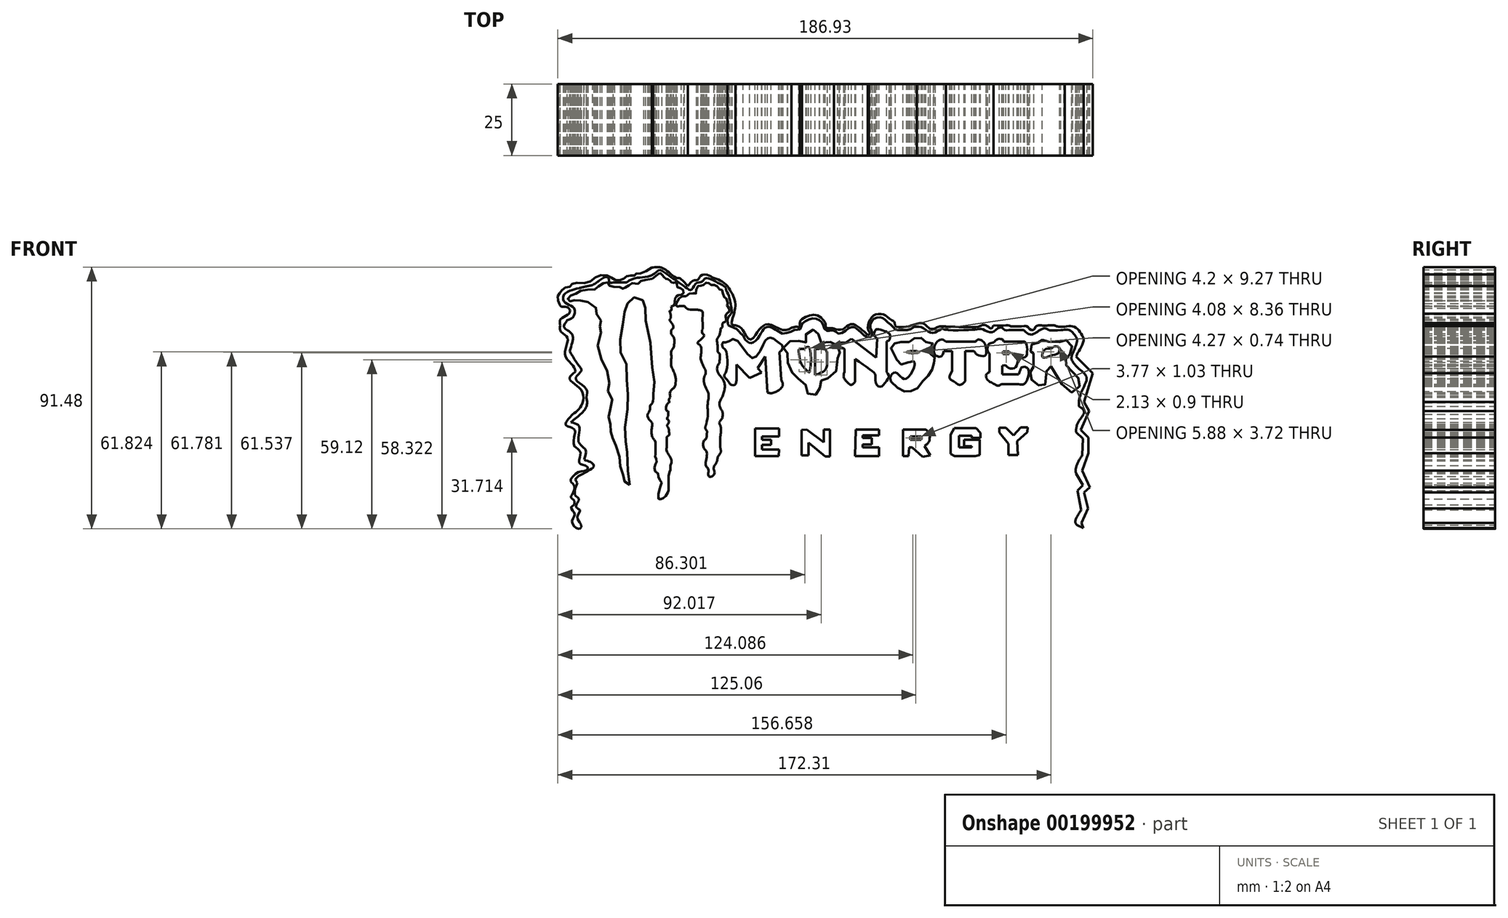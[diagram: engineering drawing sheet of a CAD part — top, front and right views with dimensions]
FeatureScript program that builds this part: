
annotation { "Feature Type Name" : "Feature", "Feature Type Description" : "" }
export const myFeature = defineFeature(function(context is Context, id is Id, definition is map)
    precondition{}
    {
        {
            var Q0;
            Q0=qCreatedBy(makeId("Front.planeOp"),FACE);
            var sketch = newSketch(context, id + "F0", { "sketchPlane" : qUnion([Q0])});
            skLineSegment(sketch, "E0.bottom", {"start": v(-137.52, -64.74) * mm, "end": v(-131.73, -64.74) * mm});
            skLineSegment(sketch, "E0.top", {"start": v(-137.52, -68.4) * mm, "end": v(-131.73, -68.4) * mm});
            skLineSegment(sketch, "E0.left", {"start": v(-137.52, -64.74) * mm, "end": v(-137.52, -68.4) * mm});
            skLineSegment(sketch, "E0.right", {"start": v(-131.73, -64.74) * mm, "end": v(-131.73, -68.4) * mm});
            skSolve(sketch);
        }
        {
            var Q0;
            Q0 = qConstructionFilter(qBodyType(qCreatedBy(id + "F0" ,EDGE), BodyType.WIRE), ConstructionObject.NO);
            extrude(context, id + "F1", {"bodyType" : ToolBodyType.SURFACE, "surfaceEntities" : qUnion([Q0]), "depth" : 25 * mm});
        }
        {
            var Q0;
            Q0=qCreatedBy(makeId("Front.planeOp"),FACE);
            var sketch = newSketch(context, id + "F2", { "sketchPlane" : qUnion([Q0])});
            skPoint(sketch, "E1.start.orphan", {"position": v(0, -27.28) * mm});
            skLineSegment(sketch, "E2", {"start": v(-13.64, -32.05) * mm, "end": v(-21.83, -32.05) * mm});
            skLineSegment(sketch, "E3", {"start": v(-21.83, -32.05) * mm, "end": v(-21.83, -22.36) * mm});
            skLineSegment(sketch, "E4", {"start": v(-21.83, -22.36) * mm, "end": v(-13.54, -22.36) * mm});
            skLineSegment(sketch, "E5", {"start": v(-13.54, -22.36) * mm, "end": v(-13.54, -25.1) * mm});
            skLineSegment(sketch, "E6", {"start": v(-13.54, -25.1) * mm, "end": v(-19.44, -25.1) * mm});
            skLineSegment(sketch, "E7", {"start": v(-19.44, -25.1) * mm, "end": v(-19.44, -26.35) * mm});
            skLineSegment(sketch, "E8", {"start": v(-19.44, -26.35) * mm, "end": v(-16.23, -26.35) * mm});
            skLineSegment(sketch, "E9", {"start": v(-16.23, -26.35) * mm, "end": v(-16.23, -28.11) * mm});
            skLineSegment(sketch, "E10", {"start": v(-16.23, -28.11) * mm, "end": v(-19.44, -28.11) * mm});
            skLineSegment(sketch, "E11", {"start": v(-19.44, -28.11) * mm, "end": v(-19.44, -29.77) * mm});
            skLineSegment(sketch, "E12", {"start": v(-19.44, -29.77) * mm, "end": v(-13.54, -29.77) * mm});
            skLineSegment(sketch, "E13", {"start": v(-13.54, -29.77) * mm, "end": v(-13.64, -32.05) * mm});
            skLineSegment(sketch, "E14", {"start": v(-5.6, -22.83) * mm, "end": v(-5.6, -31.7) * mm});
            skLineSegment(sketch, "E15", {"start": v(-5.6, -31.7) * mm, "end": v(-3.2, -31.7) * mm});
            skLineSegment(sketch, "E16", {"start": v(-3.2, -31.7) * mm, "end": v(-3.2, -27.34) * mm});
            skLineSegment(sketch, "E17", {"start": v(-3.2, -27.34) * mm, "end": v(2.65, -32.16) * mm});
            skLineSegment(sketch, "E18", {"start": v(2.65, -32.16) * mm, "end": v(4.3, -32.16) * mm});
            skLineSegment(sketch, "E19", {"start": v(4.3, -32.16) * mm, "end": v(4.3, -22.78) * mm});
            skLineSegment(sketch, "E20", {"start": v(4.3, -22.78) * mm, "end": v(2.08, -22.78) * mm});
            skLineSegment(sketch, "E21", {"start": v(2.08, -22.78) * mm, "end": v(2.08, -27.18) * mm});
            skLineSegment(sketch, "E22", {"start": v(2.08, -27.18) * mm, "end": v(-3.83, -22.78) * mm});
            skLineSegment(sketch, "E23", {"start": v(-3.83, -22.78) * mm, "end": v(-5.6, -22.83) * mm});
            skLineSegment(sketch, "E24", {"start": v(13.32, -22.72) * mm, "end": v(21.38, -22.72) * mm});
            skLineSegment(sketch, "E25", {"start": v(21.38, -22.72) * mm, "end": v(21.38, -24.8) * mm});
            skLineSegment(sketch, "E26", {"start": v(21.38, -24.8) * mm, "end": v(15.7, -24.8) * mm});
            skLineSegment(sketch, "E27", {"start": v(15.7, -24.8) * mm, "end": v(15.7, -25.63) * mm});
            skLineSegment(sketch, "E28", {"start": v(15.7, -25.63) * mm, "end": v(18.9, -25.63) * mm});
            skLineSegment(sketch, "E29", {"start": v(18.9, -25.63) * mm, "end": v(18.9, -27.9) * mm});
            skLineSegment(sketch, "E30", {"start": v(18.9, -27.9) * mm, "end": v(15.78, -27.9) * mm});
            skLineSegment(sketch, "E31", {"start": v(15.78, -27.9) * mm, "end": v(15.78, -28.91) * mm});
            skLineSegment(sketch, "E32", {"start": v(15.78, -28.91) * mm, "end": v(21.38, -28.91) * mm});
            skLineSegment(sketch, "E33", {"start": v(21.38, -28.91) * mm, "end": v(21.38, -32.03) * mm});
            skLineSegment(sketch, "E34", {"start": v(21.38, -32.03) * mm, "end": v(13.11, -32.03) * mm});
            skLineSegment(sketch, "E35", {"start": v(13.11, -32.03) * mm, "end": v(13.32, -22.72) * mm});
            skLineSegment(sketch, "E36", {"start": v(31.73, -32.05) * mm, "end": v(29.87, -32.05) * mm});
            skLineSegment(sketch, "E37", {"start": v(29.87, -32.05) * mm, "end": v(29.87, -22.72) * mm});
            skLineSegment(sketch, "E38", {"start": v(29.87, -22.72) * mm, "end": v(37.84, -22.72) * mm});
            skFitSpline(sketch, "E39", {"points": [v(37.84, -22.72) * mm, v(39.06, -24.2) * mm, v(39.12, -25.83) * mm, v(38.77, -27.23) * mm, v(37.31, -28.45) * mm], "startDerivative": vector(5.78, -5.29) * mm, "endDerivative": vector(-6.62, -4.3) * mm});
            skLineSegment(sketch, "E40", {"start": v(37.31, -28.45) * mm, "end": v(39.3, -31.77) * mm});
            skLineSegment(sketch, "E41", {"start": v(39.3, -31.77) * mm, "end": v(36.67, -32.23) * mm});
            skLineSegment(sketch, "E42", {"start": v(36.67, -32.23) * mm, "end": v(32.95, -28.92) * mm});
            skLineSegment(sketch, "E43", {"start": v(32.95, -28.92) * mm, "end": v(32.02, -28.92) * mm});
            skLineSegment(sketch, "E44", {"start": v(32.02, -28.92) * mm, "end": v(31.73, -32.05) * mm});
            skLineSegment(sketch, "E45", {"start": v(55.12, -32.05) * mm, "end": v(47.86, -32.05) * mm});
            skLineSegment(sketch, "E46", {"start": v(47.86, -32.05) * mm, "end": v(46.4, -31.25) * mm});
            skLineSegment(sketch, "E47", {"start": v(46.4, -31.25) * mm, "end": v(46.4, -24.47) * mm});
            skLineSegment(sketch, "E48", {"start": v(46.4, -24.47) * mm, "end": v(47.68, -22.16) * mm});
            skLineSegment(sketch, "E49", {"start": v(47.68, -22.16) * mm, "end": v(55.4, -22.16) * mm});
            skLineSegment(sketch, "E50", {"start": v(55.4, -22.16) * mm, "end": v(56.85, -23.85) * mm});
            skLineSegment(sketch, "E51", {"start": v(56.85, -23.85) * mm, "end": v(56.85, -25.72) * mm});
            skLineSegment(sketch, "E52", {"start": v(56.85, -25.72) * mm, "end": v(53.88, -25.72) * mm});
            skLineSegment(sketch, "E53", {"start": v(53.88, -25.72) * mm, "end": v(53.88, -24.92) * mm});
            skLineSegment(sketch, "E54", {"start": v(53.88, -24.92) * mm, "end": v(49.44, -24.92) * mm});
            skLineSegment(sketch, "E55", {"start": v(49.44, -24.92) * mm, "end": v(49.44, -29) * mm});
            skLineSegment(sketch, "E56", {"start": v(49.44, -29) * mm, "end": v(53.88, -29) * mm});
            skLineSegment(sketch, "E57", {"start": v(53.88, -29) * mm, "end": v(53.88, -28.55) * mm});
            skLineSegment(sketch, "E58", {"start": v(53.88, -28.55) * mm, "end": v(51.18, -28.55) * mm});
            skLineSegment(sketch, "E59", {"start": v(51.18, -28.55) * mm, "end": v(51.18, -26.3) * mm});
            skLineSegment(sketch, "E60", {"start": v(51.18, -26.3) * mm, "end": v(56.62, -26.3) * mm});
            skLineSegment(sketch, "E61", {"start": v(56.62, -26.3) * mm, "end": v(56.62, -31.63) * mm});
            skLineSegment(sketch, "E62", {"start": v(56.62, -31.63) * mm, "end": v(55.12, -32.05) * mm});
            skLineSegment(sketch, "E63", {"start": v(69.9, -31.63) * mm, "end": v(66.64, -31.63) * mm});
            skLineSegment(sketch, "E64", {"start": v(66.64, -31.63) * mm, "end": v(66.64, -27.74) * mm});
            skLineSegment(sketch, "E65", {"start": v(66.64, -27.74) * mm, "end": v(63.46, -23.72) * mm});
            skLineSegment(sketch, "E66", {"start": v(63.46, -23.72) * mm, "end": v(63.46, -22.15) * mm});
            skLineSegment(sketch, "E67", {"start": v(63.46, -22.15) * mm, "end": v(65.72, -22.15) * mm});
            skLineSegment(sketch, "E68", {"start": v(65.72, -22.15) * mm, "end": v(68.42, -24.71) * mm});
            skLineSegment(sketch, "E69", {"start": v(68.42, -24.71) * mm, "end": v(70.99, -22) * mm});
            skLineSegment(sketch, "E70", {"start": v(70.99, -22) * mm, "end": v(73.33, -22) * mm});
            skLineSegment(sketch, "E71", {"start": v(73.33, -22) * mm, "end": v(73.2, -23.63) * mm});
            skLineSegment(sketch, "E72", {"start": v(73.2, -23.63) * mm, "end": v(69.74, -26.81) * mm});
            skLineSegment(sketch, "E73", {"start": v(69.74, -26.81) * mm, "end": v(69.9, -31.63) * mm});
            skLineSegment(sketch, "E74.bottom", {"start": v(32.38, -25.2) * mm, "end": v(36.14, -25.2) * mm});
            skLineSegment(sketch, "E74.top", {"start": v(32.38, -26.23) * mm, "end": v(36.14, -26.23) * mm});
            skLineSegment(sketch, "E74.left", {"start": v(32.38, -25.2) * mm, "end": v(32.38, -26.23) * mm});
            skLineSegment(sketch, "E74.right", {"start": v(36.14, -25.2) * mm, "end": v(36.14, -26.23) * mm});
            skFitSpline(sketch, "E75", {"points": [v(3.5, -4.78) * mm, v(1.8, -5.19) * mm, v(0.6, -6.8) * mm, v(0.68, -9.22) * mm, v(-1.5, -10.84) * mm, v(-3.52, -10.03) * mm, v(-4.24, -6.96) * mm, v(-6.9, -4.86) * mm, v(-9, -2.69) * mm, v(-10.54, 1.1) * mm, v(-10.62, 4.25) * mm, v(-11.83, 5.63) * mm, v(-11.9, 6.51) * mm, v(-7.3, 8.77) * mm, v(-6.02, 7.64) * mm, v(-3.92, 7.97) * mm, v(-4.08, 10.7) * mm, v(-1.81, 12.14) * mm, v(0, 11.62) * mm, v(0.62, 8.04) * mm, v(3.37, 7.78) * mm, v(5.87, 7.52) * mm, v(7.54, 5.47) * mm, v(7.73, 4.13) * mm, v(7.09, 3.43) * mm, v(6.83, -1.5) * mm, v(3.5, -4.78) * mm]});
            skFitSpline(sketch, "E76", {"points": [v(-3.3, -2.5) * mm, v(-5.32, -0.43) * mm, v(-6.25, 1.83) * mm, v(-6.53, 4.09) * mm, v(-6.49, 5.34) * mm, v(-4.71, 5.46) * mm, v(-4.1, 5.94) * mm, v(-2.94, 5.94) * mm, v(-2.86, -2.65) * mm, v(-3.3, -2.5) * mm]});
            skLineSegment(sketch, "E77", {"start": v(-0.88, 5.34) * mm, "end": v(-0.88, -3.74) * mm});
            skFitSpline(sketch, "E78", {"points": [v(-0.88, -3.74) * mm, v(1.82, -2.53) * mm, v(3.07, -1.04) * mm, v(3.32, 2.51) * mm, v(3.2, 4.4) * mm, v(2.59, 5.38) * mm, v(0.98, 5.54) * mm, v(-0.88, 5.34) * mm], "startDerivative": vector(17.33, 6.66) * mm, "endDerivative": vector(-13.48, -1.69) * mm});
            skLineSegment(sketch, "E79", {"start": v(13, 1.9) * mm, "end": v(13, -6.13) * mm});
            skFitSpline(sketch, "E80", {"points": [v(13, -6.13) * mm, v(11.7, -7.08) * mm, v(9.88, -5.7) * mm, v(9.07, -4.24) * mm, v(9.32, -2.56) * mm], "startDerivative": vector(-5.12, -6.15) * mm, "endDerivative": vector(2, 7.23) * mm});
            skLineSegment(sketch, "E81", {"start": v(9.32, -2.56) * mm, "end": v(9.32, 4.81) * mm});
            skFitSpline(sketch, "E82", {"points": [v(9.32, 4.81) * mm, v(9.32, 5.45) * mm, v(8.29, 5.83) * mm, v(7.55, 6.15) * mm, v(7.84, 7.43) * mm, v(9.8, 7.56) * mm], "startDerivative": vector(1.21, 4.66) * mm, "endDerivative": vector(8.72, -1.45) * mm});
            skLineSegment(sketch, "E83", {"start": v(9.8, 7.56) * mm, "end": v(11.78, 9.02) * mm});
            skLineSegment(sketch, "E84", {"start": v(11.78, 9.02) * mm, "end": v(20.42, 2.42) * mm});
            skLineSegment(sketch, "E85", {"start": v(20.42, 2.42) * mm, "end": v(20.78, 9.02) * mm});
            skFitSpline(sketch, "E86", {"points": [v(20.78, 9.02) * mm, v(19.76, 10.24) * mm, v(19.97, 11.77) * mm, v(20.78, 12.38) * mm, v(23.58, 11.67) * mm, v(25.2, 10.5) * mm, v(25, 8.52) * mm, v(24.14, 8.16) * mm], "startDerivative": vector(-9.3, 7.78) * mm, "endDerivative": vector(-8.95, -0.97) * mm});
            skLineSegment(sketch, "E87", {"start": v(24.14, 8.16) * mm, "end": v(24.14, -2.67) * mm});
            skFitSpline(sketch, "E88", {"points": [v(24.14, -2.67) * mm, v(24.85, -4.1) * mm, v(23.68, -6.23) * mm, v(22.05, -7.75) * mm, v(20.48, -6.84) * mm, v(20.17, -3.84) * mm, v(19.5, -2.67) * mm, v(13, 1.9) * mm], "startDerivative": vector(9.85, -12.2) * mm, "endDerivative": vector(-32.83, 21.87) * mm});
            skFitSpline(sketch, "E89", {"points": [v(25.58, -6) * mm, v(25.5, -4.1) * mm, v(27.4, -2.82) * mm, v(30.6, -5.05) * mm, v(33.92, 0.65) * mm, v(31.55, 0.71) * mm], "startDerivative": vector(-3.3, 12.09) * mm, "endDerivative": vector(-18.92, -5.85) * mm});
            skFitSpline(sketch, "E90", {"points": [v(31.55, 0.71) * mm, v(29.32, 0) * mm, v(27.8, 1.3) * mm, v(26.98, 3.23) * mm, v(25.76, 4.9) * mm, v(25.92, 6.69) * mm, v(27.5, 7.6) * mm, v(29.52, 7.86) * mm, v(32.52, 8.11) * mm, v(33.92, 9.28) * mm, v(36.28, 9.28) * mm, v(37.6, 7.9) * mm, v(39.84, 7.65) * mm, v(40.15, 5.98) * mm, v(38.57, 4.66) * mm, v(39.7, 3.64) * mm, v(40.96, 2.11) * mm, v(40.7, 0.71) * mm, v(40.1, -1.24) * mm, v(38.98, -3.43) * mm, v(37, -5.46) * mm, v(34.96, -8.1) * mm, v(32.83, -9.17) * mm, v(30.8, -9.48) * mm, v(28.36, -8.5) * mm, v(25.58, -6) * mm], "startDerivative": vector(-56.1, -30.21) * mm, "endDerivative": vector(-52.2, 53.3) * mm});
            skLineSegment(sketch, "E91", {"start": v(51.53, -5.87) * mm, "end": v(51.53, 4.76) * mm});
            skLineSegment(sketch, "E92", {"start": v(51.53, 4.76) * mm, "end": v(54.58, 4.76) * mm});
            skFitSpline(sketch, "E93", {"points": [v(54.58, 4.76) * mm, v(56, 3.33) * mm, v(58.55, 3.23) * mm, v(58.85, 5.27) * mm, v(58.4, 7.3) * mm, v(57.53, 8.26) * mm, v(56.1, 8.77) * mm, v(55.24, 8.01) * mm], "startDerivative": vector(7.12, -10.63) * mm, "endDerivative": vector(-6.49, -9.06) * mm});
            skLineSegment(sketch, "E94", {"start": v(55.24, 8.01) * mm, "end": v(44.82, 8.01) * mm});
            skFitSpline(sketch, "E95", {"points": [v(44.82, 8.01) * mm, v(43.4, 8.77) * mm, v(41.83, 8.01) * mm, v(40.91, 6.69) * mm, v(40.7, 5.47) * mm, v(40.8, 3.69) * mm, v(41.98, 2.83) * mm, v(43.25, 2.88) * mm, v(44.06, 4.7) * mm], "startDerivative": vector(-10.85, 8.8) * mm, "endDerivative": vector(4.19, 16.26) * mm});
            skLineSegment(sketch, "E96", {"start": v(44.06, 4.7) * mm, "end": v(46.9, 4.7) * mm});
            skLineSegment(sketch, "E97", {"start": v(46.9, 4.7) * mm, "end": v(46.9, -2.1) * mm});
            skLineSegment(sketch, "E98", {"start": v(46.9, -2.1) * mm, "end": v(46.15, -3.78) * mm});
            skFitSpline(sketch, "E99", {"points": [v(46.15, -3.78) * mm, v(46.15, -4.9) * mm, v(47.57, -5.92) * mm, v(49.7, -7.09) * mm, v(51.53, -5.87) * mm], "startDerivative": vector(-1.29, -6.23) * mm, "endDerivative": vector(6.5, 6.73) * mm});
            skEllipse(sketch, "E100", {"center": v(33.29, 4.35) * mm, "majorRadius": 2.13 * mm, "minorRadius": 0.37 * mm, "majorAxis": v(-1, 0)});
            skLineSegment(sketch, "E101", {"start": v(60.02, -2.61) * mm, "end": v(60.02, 3.8) * mm});
            skFitSpline(sketch, "E102", {"points": [v(60.02, 3.8) * mm, v(59.46, 4.6) * mm, v(59.41, 6.33) * mm, v(60.02, 7.35) * mm, v(61.34, 7.7) * mm, v(62.77, 8.77) * mm, v(64.55, 8.77) * mm, v(65, 7.96) * mm], "startDerivative": vector(-5.38, 5.66) * mm, "endDerivative": vector(2.12, -7.98) * mm});
            skLineSegment(sketch, "E103", {"start": v(65, 7.96) * mm, "end": v(72.32, 7.96) * mm});
            skFitSpline(sketch, "E104", {"points": [v(72.32, 7.96) * mm, v(73.09, 6.69) * mm, v(73.19, 4.4) * mm, v(72.68, 2.67) * mm, v(70.65, 2.27) * mm, v(70.24, 2.01) * mm, v(69.32, -0.68) * mm, v(68.46, -1.34) * mm, v(66.68, -1.19) * mm, v(65.82, -0.38) * mm, v(64.55, -0.43) * mm], "startDerivative": vector(9.43, -11.65) * mm, "endDerivative": vector(-15.75, -3.65) * mm});
            skLineSegment(sketch, "E105", {"start": v(64.55, -0.43) * mm, "end": v(64.55, -3.38) * mm});
            skLineSegment(sketch, "E106", {"start": v(64.55, -3.38) * mm, "end": v(70.19, -3.38) * mm});
            skFitSpline(sketch, "E107", {"points": [v(70.19, -3.38) * mm, v(70.8, -1.95) * mm, v(71.36, -0.99) * mm, v(73.09, -1.04) * mm, v(73.75, -2.61) * mm, v(73.29, -5.05) * mm, v(72.73, -6.22) * mm, v(71.71, -6.98) * mm, v(70.19, -6.83) * mm], "startDerivative": vector(5.45, 11.63) * mm, "endDerivative": vector(-12.95, 3.3) * mm});
            skLineSegment(sketch, "E108", {"start": v(70.19, -6.83) * mm, "end": v(64.34, -6.83) * mm});
            skFitSpline(sketch, "E109", {"points": [v(64.34, -6.83) * mm, v(62.97, -7.4) * mm, v(61.75, -6.83) * mm, v(59.51, -5.51) * mm, v(58.85, -3.73) * mm, v(60.02, -2.61) * mm], "startDerivative": vector(-7.82, -4.67) * mm, "endDerivative": vector(8.05, 4.95) * mm});
            skLineSegment(sketch, "E110.bottom", {"start": v(64.8, 4.56) * mm, "end": v(66.92, 4.56) * mm});
            skLineSegment(sketch, "E110.top", {"start": v(64.8, 3.66) * mm, "end": v(66.92, 3.66) * mm});
            skLineSegment(sketch, "E110.left", {"start": v(64.8, 4.56) * mm, "end": v(64.8, 3.66) * mm});
            skLineSegment(sketch, "E110.right", {"start": v(66.92, 4.56) * mm, "end": v(66.92, 3.66) * mm});
            skFitSpline(sketch, "E111", {"points": [v(75.4, 3.92) * mm, v(75.17, 4.58) * mm, v(74.49, 4.56) * mm, v(74.3, 6.2) * mm, v(75.86, 7.6) * mm, v(77.08, 7.64) * mm, v(77.48, 8.3) * mm, v(79.77, 8.47) * mm, v(80.47, 8) * mm, v(84.73, 7.96) * mm, v(86.3, 8.64) * mm, v(88.87, 6.8) * mm, v(88.27, 4.41) * mm, v(87.85, 2.62) * mm, v(86.44, 1.76) * mm, v(86.4, 0.4) * mm, v(92.16, -6.53) * mm, v(90.32, -8.41) * mm, v(87.72, -9.74) * mm, v(80.66, 0) * mm, v(79.72, -6.02) * mm, v(78.66, -7.6) * mm, v(76.05, -6.61) * mm, v(74.34, -4.48) * mm, v(74.38, -2.51) * mm, v(75.1, -1.91) * mm, v(75.4, 3.92) * mm]});
            skFitSpline(sketch, "E112", {"points": [v(78.57, 2.53) * mm, v(79.51, 5.35) * mm, v(81.65, 5.7) * mm, v(82.67, 6.34) * mm, v(84.17, 6) * mm, v(84.51, 5.05) * mm, v(84, 3.92) * mm, v(81.86, 3.22) * mm, v(78.57, 2.53) * mm]});
            skLineSegment(sketch, "E113", {"start": v(-28.35, -5.42) * mm, "end": v(-28.35, 0) * mm});
            skLineSegment(sketch, "E114", {"start": v(-28.35, 0) * mm, "end": v(-23.74, -4.68) * mm});
            skLineSegment(sketch, "E115", {"start": v(-23.74, -4.68) * mm, "end": v(-19.53, -2.78) * mm});
            skLineSegment(sketch, "E116", {"start": v(-19.53, -2.78) * mm, "end": v(-20.95, -1.22) * mm});
            skLineSegment(sketch, "E117", {"start": v(-20.95, -1.22) * mm, "end": v(-18.38, 2.79) * mm});
            skLineSegment(sketch, "E118", {"start": v(-18.38, 2.79) * mm, "end": v(-17.56, -9.83) * mm});
            skFitSpline(sketch, "E119", {"points": [v(-17.56, -9.83) * mm, v(-15.26, -9.83) * mm, v(-12.27, -7.46) * mm, v(-12.74, -5.29) * mm], "startDerivative": vector(6.9, -1.35) * mm, "endDerivative": vector(-3.74, 7.1) * mm});
            skLineSegment(sketch, "E120", {"start": v(-12.74, -5.29) * mm, "end": v(-13.36, 4.28) * mm});
            skFitSpline(sketch, "E121", {"points": [v(-13.36, 4.28) * mm, v(-12.31, 5.41) * mm, v(-12.48, 6.8) * mm, v(-13.6, 7.67) * mm, v(-15.8, 9.2) * mm, v(-17.42, 9.14) * mm, v(-18.93, 7.26) * mm, v(-22.71, 2.19) * mm, v(-28.88, 8.87) * mm, v(-31.87, 7.72) * mm, v(-33.08, 7.78) * mm, v(-33.44, 6.51) * mm, v(-32.32, 5.27) * mm], "startDerivative": vector(20.04, 15.2) * mm, "endDerivative": vector(21.72, -15.34) * mm});
            skFitSpline(sketch, "E122", {"points": [v(-32.32, 5.27) * mm, v(-31.8, 4) * mm, v(-31.91, -2.31) * mm, v(-32.7, -4.07) * mm, v(-31.49, -5.46) * mm, v(-30.43, -6.92) * mm, v(-28.94, -7.06) * mm, v(-28.35, -5.42) * mm], "startDerivative": vector(5, -7.8) * mm, "endDerivative": vector(2, 15.9) * mm});
            skFitSpline(sketch, "E123", {"points": [v(86.28, 13.2) * mm, v(89.51, 13.26) * mm, v(91.89, 11.04) * mm, v(92.9, 8.45) * mm, v(91.1, 4.42) * mm, v(90.3, 2.84) * mm], "startDerivative": vector(16.55, 3.2) * mm, "endDerivative": vector(-3.97, -8.8) * mm});
            skLineSegment(sketch, "E124", {"start": v(90.3, 2.84) * mm, "end": v(96.13, -3.05) * mm});
            skLineSegment(sketch, "E125", {"start": v(96.13, -3.05) * mm, "end": v(93.1, -13.12) * mm});
            skLineSegment(sketch, "E126", {"start": v(93.1, -13.12) * mm, "end": v(94.83, -16.28) * mm});
            skLineSegment(sketch, "E127", {"start": v(94.83, -16.28) * mm, "end": v(91.89, -22.9) * mm});
            skLineSegment(sketch, "E128", {"start": v(91.89, -22.9) * mm, "end": v(94.62, -25.48) * mm});
            skLineSegment(sketch, "E129", {"start": v(94.62, -25.48) * mm, "end": v(94.62, -31.02) * mm});
            skLineSegment(sketch, "E130", {"start": v(94.62, -31.02) * mm, "end": v(92.46, -37.13) * mm});
            skLineSegment(sketch, "E131", {"start": v(92.46, -37.13) * mm, "end": v(95.12, -42.88) * mm});
            skLineSegment(sketch, "E132", {"start": v(95.12, -42.88) * mm, "end": v(93.1, -44.75) * mm});
            skLineSegment(sketch, "E133", {"start": v(93.1, -44.75) * mm, "end": v(94.4, -50.36) * mm});
            skLineSegment(sketch, "E134", {"start": v(94.4, -50.36) * mm, "end": v(92.24, -55.39) * mm});
            skLineSegment(sketch, "E135", {"start": v(92.24, -55.39) * mm, "end": v(92.75, -57.18) * mm});
            skLineSegment(sketch, "E136", {"start": v(92.75, -57.18) * mm, "end": v(90.66, -56.18) * mm});
            skPoint(sketch, "E137.2.internal.snap0", {"position": v(91.7, -56.68) * mm});
            skFitSpline(sketch, "E138", {"points": [v(90.66, -56.18) * mm, v(90.02, -55) * mm, v(92.07, -50.8) * mm], "startDerivative": vector(-2.73, 2.84) * mm, "endDerivative": vector(4.79, 7.46) * mm});
            skLineSegment(sketch, "E139", {"start": v(92.07, -50.8) * mm, "end": v(90.77, -44.03) * mm});
            skLineSegment(sketch, "E140", {"start": v(90.77, -44.03) * mm, "end": v(92.68, -42.14) * mm});
            skLineSegment(sketch, "E141", {"start": v(92.68, -42.14) * mm, "end": v(90.23, -38.07) * mm});
            skFitSpline(sketch, "E142", {"points": [v(90.23, -38.07) * mm, v(90.23, -36.29) * mm, v(90.9, -34.27) * mm, v(92.47, -31.65) * mm], "startDerivative": vector(-0.4, 6.03) * mm, "endDerivative": vector(4.52, 6.94) * mm});
            skLineSegment(sketch, "E143", {"start": v(92.47, -31.65) * mm, "end": v(92.65, -25.9) * mm});
            skLineSegment(sketch, "E144", {"start": v(92.65, -25.9) * mm, "end": v(90.31, -23.64) * mm});
            skFitSpline(sketch, "E145", {"points": [v(90.31, -23.64) * mm, v(90.31, -22.52) * mm, v(90.58, -21.24) * mm], "startDerivative": vector(-0.12, 2.3) * mm, "endDerivative": vector(0.65, 2.5) * mm});
            skFitSpline(sketch, "E146", {"points": [v(90.58, -21.24) * mm, v(91.45, -19.47) * mm, v(93.1, -16.52) * mm, v(91.34, -14.62) * mm], "startDerivative": vector(2.12, 5.59) * mm, "endDerivative": vector(-7.8, 5.1) * mm});
            skPoint(sketch, "E147.3.internal.snap0", {"position": v(93.97, -14.7) * mm});
            skFitSpline(sketch, "E147", {"points": [v(91.34, -14.62) * mm, v(91.34, -12.76) * mm, v(92.2, -9.5) * mm, v(93.97, -5.07) * mm, v(93.23, -3.15) * mm, v(91.34, -1.55) * mm], "startDerivative": vector(-0.57, 10.85) * mm, "endDerivative": vector(-11, 8.15) * mm});
            skFitSpline(sketch, "E148", {"points": [v(91.34, -1.55) * mm, v(88.73, 1.8) * mm, v(89.1, 3.93) * mm], "startDerivative": vector(-6.02, 5.91) * mm, "endDerivative": vector(1.96, 5) * mm});
            skFitSpline(sketch, "E149", {"points": [v(89.1, 3.93) * mm, v(90.31, 6.93) * mm, v(90.58, 8.96) * mm, v(89.5, 10.74) * mm, v(87.92, 12) * mm, v(84.92, 12.06) * mm], "startDerivative": vector(5.9, 13.53) * mm, "endDerivative": vector(-14.9, -1.56) * mm});
            skFitSpline(sketch, "E150", {"points": [v(84.92, 12.06) * mm, v(80.75, 12.06) * mm, v(79.77, 12.62) * mm, v(78.62, 12.5) * mm, v(77.15, 11.75) * mm, v(75.93, 10.93) * mm, v(74.42, 10.46) * mm, v(72.95, 11.18) * mm, v(72.05, 12.06) * mm], "startDerivative": vector(-25.23, -2.35) * mm, "endDerivative": vector(-7.45, 8.11) * mm});
            skFitSpline(sketch, "E151", {"points": [v(72.05, 12.06) * mm, v(69.78, 12.06) * mm, v(67.05, 12.06) * mm, v(65.29, 12.06) * mm, v(64.14, 13.01) * mm, v(62.34, 12.18) * mm, v(60.69, 11.25) * mm, v(58.17, 12.06) * mm, v(56.84, 12.5) * mm, v(54.94, 12.18) * mm], "startDerivative": vector(-18.43, -0.3) * mm, "endDerivative": vector(-18.73, -4.91) * mm});
            skFitSpline(sketch, "E152", {"points": [v(54.94, 12.18) * mm, v(54.07, 12.18) * mm, v(44.44, 12.18) * mm, v(43.36, 12.54) * mm, v(41.74, 11.54) * mm, v(39.4, 11.14) * mm, v(36.35, 13.01) * mm, v(33.73, 13.16) * mm], "startDerivative": vector(-6.06, 0.36) * mm, "endDerivative": vector(-18.64, -2.44) * mm});
            skFitSpline(sketch, "E153", {"points": [v(33.73, 13.16) * mm, v(31.82, 12.18) * mm, v(27.11, 12.18) * mm], "startDerivative": vector(-4.1, -2.92) * mm, "endDerivative": vector(-8.83, 0.73) * mm});
            skFitSpline(sketch, "E154", {"points": [v(27.11, 12.18) * mm, v(25.68, 13.77) * mm, v(23.7, 15.42) * mm, v(22.33, 16.4) * mm, v(20.72, 16.43) * mm, v(19.1, 15.42) * mm, v(18.34, 13.16) * mm, v(18.81, 11.77) * mm, v(19.03, 10.78) * mm, v(18.74, 9.78) * mm, v(17.12, 9.63) * mm, v(14.96, 11.47) * mm, v(13.6, 12.58) * mm, v(12.45, 13.16) * mm, v(10.8, 12.76) * mm], "startDerivative": vector(-16.66, 20.22) * mm, "endDerivative": vector(-24.78, -9.61) * mm});
            skFitSpline(sketch, "E155", {"points": [v(10.8, 12.76) * mm, v(8.9, 11.3) * mm, v(6.91, 10.9) * mm, v(6.15, 11.77) * mm, v(4.05, 11.77) * mm, v(3.2, 11.77) * mm, v(2.23, 12.76) * mm, v(1.63, 14.48) * mm, v(0.42, 15.53) * mm, v(-1.44, 16.14) * mm, v(-3.37, 15.65) * mm, v(-5.31, 14.4) * mm, v(-5.84, 13.16) * mm, v(-6.4, 12.18) * mm, v(-7.73, 12.18) * mm, v(-9.7, 11.34) * mm, v(-12.37, 10.85) * mm], "startDerivative": vector(-23.29, -21.5) * mm, "endDerivative": vector(-35.58, -3.08) * mm});
            skFitSpline(sketch, "E156", {"points": [v(-12.37, 10.85) * mm, v(-14.07, 11.78) * mm, v(-15.4, 12.55) * mm, v(-16.9, 13.15) * mm, v(-18.46, 12.75) * mm, v(-19.88, 10.85) * mm, v(-22.42, 7.75) * mm, v(-24.6, 7.99) * mm, v(-26.09, 10.17) * mm], "startDerivative": vector(-14.95, 8.07) * mm, "endDerivative": vector(-9, 18.37) * mm});
            skFitSpline(sketch, "E157", {"points": [v(-26.09, 10.17) * mm, v(-27.34, 11.38) * mm, v(-28.19, 12.3) * mm, v(-29.96, 13.2) * mm, v(-31.3, 13.68) * mm], "startDerivative": vector(-5.24, 4.7) * mm, "endDerivative": vector(-5.26, 1.84) * mm});
            skFitSpline(sketch, "E158", {"points": [v(-31.3, 13.68) * mm, v(-31.3, 16.42) * mm, v(-30.12, 17.95) * mm, v(-30.12, 19.85) * mm, v(-30.57, 22.1) * mm, v(-31.3, 24.65) * mm, v(-31.94, 26.1) * mm, v(-32.14, 26.83) * mm, v(-33.31, 27.76) * mm], "startDerivative": vector(-3.32, 20.04) * mm, "endDerivative": vector(-13.09, 8.19) * mm});
            skFitSpline(sketch, "E159", {"points": [v(-33.31, 27.76) * mm, v(-35.9, 29.13) * mm, v(-38.27, 30.18) * mm, v(-39.77, 29.74) * mm, v(-40.5, 28.85) * mm, v(-42.1, 28.6) * mm, v(-43.4, 27.07) * mm, v(-44.37, 26.02) * mm, v(-45.58, 26.63) * mm, v(-47.68, 28.08) * mm], "startDerivative": vector(-18.59, 9.55) * mm, "endDerivative": vector(-16.96, 11.38) * mm});
            skFitSpline(sketch, "E160", {"points": [v(-47.68, 28.08) * mm, v(-49.2, 29.17) * mm, v(-50.54, 30.06) * mm, v(-52.6, 31.55) * mm, v(-54.33, 32.76) * mm, v(-55.42, 33) * mm, v(-57, 31.75) * mm, v(-60.22, 30.58) * mm, v(-62.16, 30.38) * mm, v(-64.62, 29.94) * mm, v(-66.68, 28.73) * mm], "startDerivative": vector(-16.76, 12.14) * mm, "endDerivative": vector(-18.17, -13.1) * mm});
            skFitSpline(sketch, "E161", {"points": [v(-66.68, 28.73) * mm, v(-69.1, 28.73) * mm, v(-71.44, 28.73) * mm], "startDerivative": vector(-4.82, 0) * mm, "endDerivative": vector(-4.7, 0) * mm});
            skFitSpline(sketch, "E162", {"points": [v(-71.44, 28.73) * mm, v(-72.73, 28.73) * mm, v(-73.1, 30.22) * mm, v(-74.27, 30.58) * mm, v(-76.12, 29.5) * mm, v(-77.17, 28.73) * mm, v(-78.58, 27.76) * mm], "startDerivative": vector(-10.38, -2.63) * mm, "endDerivative": vector(-8.48, -5.77) * mm});
            skFitSpline(sketch, "E163", {"points": [v(-78.58, 27.76) * mm, v(-81.04, 27.27) * mm, v(-83.4, 26.7) * mm], "startDerivative": vector(-4.91, -0.93) * mm, "endDerivative": vector(-4.72, -1.18) * mm});
            skFitSpline(sketch, "E164", {"points": [v(-83.4, 26.7) * mm, v(-86.22, 25.9) * mm, v(-88.71, 24.26) * mm, v(-88.57, 21.91) * mm, v(-86.65, 20.76) * mm, v(-84.97, 19.37) * mm, v(-85.36, 16.68) * mm, v(-87.47, 15.48) * mm], "startDerivative": vector(-17.93, -4.52) * mm, "endDerivative": vector(-17.34, -5.6) * mm});
            skFitSpline(sketch, "E165", {"points": [v(-87.47, 15.48) * mm, v(-88.57, 12.99) * mm, v(-85.93, 10.78) * mm, v(-86.66, 4.73) * mm], "startDerivative": vector(-7.66, -9.9) * mm, "endDerivative": vector(-5.87, -17.07) * mm});
            skFitSpline(sketch, "E166", {"points": [v(-86.66, 4.73) * mm, v(-83.4, -0.5) * mm, v(-82.62, -2.32) * mm, v(-84.59, -4.81) * mm, v(-80.94, -8.41) * mm, v(-80.85, -11.43) * mm], "startDerivative": vector(13.31, -23.05) * mm, "endDerivative": vector(-5.2, -17.08) * mm});
            skFitSpline(sketch, "E167", {"points": [v(-80.85, -11.43) * mm, v(-80.85, -14.74) * mm, v(-86.22, -20.17) * mm], "startDerivative": vector(1.77, -8.2) * mm, "endDerivative": vector(-11.6, -9.19) * mm});
            skFitSpline(sketch, "E168", {"points": [v(-86.22, -20.17) * mm, v(-83.29, -21.76) * mm, v(-83.54, -26.98) * mm, v(-81.2, -29.72) * mm, v(-81.62, -33.3) * mm], "startDerivative": vector(16.92, -3.7) * mm, "endDerivative": vector(-5.8, -16.52) * mm});
            skFitSpline(sketch, "E169", {"points": [v(-81.62, -33.3) * mm, v(-78.59, -34.63) * mm, v(-78.5, -36) * mm, v(-84.4, -39.76) * mm, v(-84.02, -41.34) * mm], "startDerivative": vector(13.8, -4.2) * mm, "endDerivative": vector(6.23, -8.26) * mm});
            skFitSpline(sketch, "E170", {"points": [v(-84.02, -41.34) * mm, v(-84.7, -45.7) * mm, v(-83.41, -47.02) * mm, v(-84.46, -49.36) * mm, v(-83.57, -50.53) * mm], "startDerivative": vector(-5.6, -15.51) * mm, "endDerivative": vector(7.4, -5.04) * mm});
            skFitSpline(sketch, "E171", {"points": [v(-83.57, -50.53) * mm, v(-83, -51.06) * mm, v(-84.02, -53.4) * mm, v(-82.6, -56.14) * mm, v(-83.09, -57.35) * mm, v(-84.78, -56.83) * mm, v(-85.8, -54.45) * mm, v(-84.82, -52.6) * mm, v(-85.59, -50.98) * mm, v(-86.22, -50.05) * mm, v(-85.1, -48.96) * mm], "startDerivative": vector(13.11, -5.86) * mm, "endDerivative": vector(17.32, 12) * mm});
            skFitSpline(sketch, "E172", {"points": [v(-85.1, -48.96) * mm, v(-85.1, -47.58) * mm, v(-86.22, -46.4) * mm, v(-85.64, -45.16) * mm, v(-85.1, -42.21) * mm, v(-86.22, -40.92) * mm, v(-86.22, -40) * mm], "startDerivative": vector(2.44, 9.43) * mm, "endDerivative": vector(1.88, 7.66) * mm});
            skFitSpline(sketch, "E173", {"points": [v(-86.22, -40) * mm, v(-83.57, -37.61) * mm, v(-81.04, -37.1) * mm, v(-80.31, -36.08) * mm, v(-81.62, -35.15) * mm, v(-83.18, -34.5) * mm, v(-83.14, -32.5) * mm, v(-82.9, -30.84) * mm, v(-84.02, -29.26) * mm, v(-85.1, -28.42) * mm, v(-85.1, -25.35) * mm], "startDerivative": vector(18.54, 22.54) * mm, "endDerivative": vector(4, 29.92) * mm});
            skFitSpline(sketch, "E174", {"points": [v(-85.1, -25.35) * mm, v(-85.1, -22.57) * mm, v(-87.9, -21.28) * mm, v(-87.86, -20.17) * mm, v(-85.64, -17.36) * mm], "startDerivative": vector(3.48, 12.33) * mm, "endDerivative": vector(8.99, 10.12) * mm});
            skFitSpline(sketch, "E175", {"points": [v(-85.64, -17.36) * mm, v(-82.88, -14.92) * mm, v(-82.42, -9.27) * mm, v(-86.64, -5.05) * mm, v(-84.66, -2.56) * mm], "startDerivative": vector(13.34, 8.3) * mm, "endDerivative": vector(15.86, 11.76) * mm});
            skFitSpline(sketch, "E176", {"points": [v(-84.66, -2.56) * mm, v(-85.21, -0.84) * mm, v(-88.26, 3.54) * mm, v(-87.4, 9.18) * mm, v(-89.79, 11.57) * mm, v(-89.9, 13.7) * mm], "startDerivative": vector(-1.03, 11.24) * mm, "endDerivative": vector(3.23, 14.6) * mm});
            skFitSpline(sketch, "E177", {"points": [v(-89.9, 13.7) * mm, v(-89.9, 15.76) * mm, v(-86.95, 17.77) * mm, v(-86.6, 19.21) * mm, v(-87.86, 20.17) * mm, v(-89.49, 20.22) * mm, v(-90.69, 22.38) * mm], "startDerivative": vector(-3.84, 13.24) * mm, "endDerivative": vector(-5.26, 15.67) * mm});
            skFitSpline(sketch, "E178", {"points": [v(-90.69, 22.38) * mm, v(-90.69, 24.15) * mm, v(-89.82, 25.2) * mm, v(-88.58, 26.8) * mm, v(-86.56, 27.22) * mm, v(-85.4, 28.47) * mm, v(-80.61, 28.52) * mm, v(-76.96, 30.92) * mm, v(-73.13, 30.96) * mm, v(-71.11, 29.77) * mm, v(-69.34, 29.48) * mm, v(-67.42, 30.3) * mm, v(-66.02, 31.2) * mm, v(-64.06, 31.01) * mm, v(-63.63, 31.68) * mm, v(-61.95, 31.83) * mm, v(-57.92, 33.94) * mm], "startDerivative": vector(-5.17, 36.05) * mm, "endDerivative": vector(48.02, 33.2) * mm});
            skFitSpline(sketch, "E179", {"points": [v(-57.61, 33.94) * mm, v(-54.75, 33.94) * mm, v(-52.52, 32.63) * mm, v(-49.23, 30.2) * mm, v(-48.25, 30.16) * mm, v(-45.43, 27.38) * mm], "startDerivative": vector(15.02, 1.36) * mm, "endDerivative": vector(13.37, -16.1) * mm});
            skFitSpline(sketch, "E180", {"points": [v(-45.43, 27.38) * mm, v(-43.3, 29.43) * mm, v(-41.8, 29.68) * mm, v(-40.8, 31.13) * mm, v(-38.17, 31.2) * mm, v(-36.4, 30.32) * mm, v(-33.78, 29.27) * mm, v(-31.52, 27.38) * mm], "startDerivative": vector(12.74, 17.03) * mm, "endDerivative": vector(12.98, -13.29) * mm});
            skFitSpline(sketch, "E181", {"points": [v(-31.52, 27.38) * mm, v(-29.26, 23.38) * mm, v(-28.81, 19.8) * mm, v(-29.7, 16.24) * mm, v(-29.96, 14.1) * mm, v(-28.73, 13.7) * mm], "startDerivative": vector(10.58, -15.9) * mm, "endDerivative": vector(11.58, -1.01) * mm});
            skFitSpline(sketch, "E182", {"points": [v(-28.73, 13.7) * mm, v(-27.24, 13.2) * mm, v(-25.87, 11.44) * mm, v(-23.53, 8.74) * mm, v(-21.23, 11.12) * mm, v(-19.41, 13.2) * mm, v(-17.11, 14.06) * mm, v(-12.15, 12.09) * mm, v(-9.16, 12.85) * mm], "startDerivative": vector(17.5, -3.76) * mm, "endDerivative": vector(21.34, 11.53) * mm});
            skFitSpline(sketch, "E183", {"points": [v(-9.16, 12.85) * mm, v(-7.27, 13.16) * mm, v(-6.3, 13.16) * mm, v(-6.22, 14.75) * mm, v(-5.45, 15.92) * mm], "startDerivative": vector(6.78, 1.84) * mm, "endDerivative": vector(4.17, 3.94) * mm});
            skFitSpline(sketch, "E184", {"points": [v(-5.45, 15.92) * mm, v(-2.79, 17.17) * mm, v(0, 17.13) * mm, v(2.01, 15.48) * mm, v(2.7, 14.35) * mm, v(2.94, 12.85) * mm, v(4.2, 12.7) * mm, v(5.72, 12.61) * mm], "startDerivative": vector(14.61, 8.33) * mm, "endDerivative": vector(11.7, -1.22) * mm});
            skFitSpline(sketch, "E185", {"points": [v(5.72, 12.61) * mm, v(7.18, 12.13) * mm, v(9.27, 12.61) * mm, v(10.65, 13.7) * mm, v(12.87, 13.98) * mm, v(14.84, 12.61) * mm, v(16.54, 11.28) * mm, v(17.63, 10.35) * mm, v(18.27, 10.88) * mm, v(17.59, 12.2) * mm, v(17.83, 14.83) * mm], "startDerivative": vector(14.5, -7.15) * mm, "endDerivative": vector(6.46, 23.73) * mm});
            skFitSpline(sketch, "E186", {"points": [v(17.83, 14.83) * mm, v(19.16, 16.8) * mm, v(20.65, 17.61) * mm, v(22.75, 17.61) * mm, v(24, 16.93) * mm, v(25.78, 15.53) * mm, v(26.87, 14.83) * mm, v(27.1, 13.5) * mm, v(28.6, 13.1) * mm, v(30.22, 13.1) * mm, v(32.52, 13.58) * mm, v(34.61, 14.26) * mm], "startDerivative": vector(12.04, 21.27) * mm, "endDerivative": vector(20.25, 7.07) * mm});
            skFitSpline(sketch, "E187", {"points": [v(34.61, 14.26) * mm, v(37.2, 14.26) * mm, v(39.13, 12.61) * mm, v(40.9, 12.61) * mm, v(42.16, 13.18) * mm, v(44.86, 13.34) * mm], "startDerivative": vector(12.73, 2.57) * mm, "endDerivative": vector(13.56, -0.24) * mm});
            skFitSpline(sketch, "E188", {"points": [v(44.86, 13.34) * mm, v(56.44, 13.34) * mm, v(57.73, 13.86) * mm, v(59.43, 13.34) * mm, v(60.56, 12.61) * mm, v(61.44, 13.66) * mm], "startDerivative": vector(35.57, -1.94) * mm, "endDerivative": vector(6, 10.74) * mm});
            skFitSpline(sketch, "E189", {"points": [v(61.44, 13.66) * mm, v(65.36, 13.66) * mm, v(66.9, 13.66) * mm, v(67.82, 13.34) * mm, v(69.51, 13.34) * mm, v(71.13, 13.34) * mm, v(73.15, 13.34) * mm, v(74.4, 12.2) * mm, v(75.6, 12.29) * mm, v(76.21, 13.34) * mm, v(78.19, 13.66) * mm], "startDerivative": vector(28.62, -0.5) * mm, "endDerivative": vector(22.28, -0.47) * mm});
            skFitSpline(sketch, "E190", {"points": [v(78.19, 13.66) * mm, v(80.65, 13.66) * mm, v(82.67, 13.66) * mm, v(83.6, 13.34) * mm, v(86.28, 13.2) * mm], "startDerivative": vector(8.75, -0.18) * mm, "endDerivative": vector(10.66, 0.07) * mm});
            skLineSegment(sketch, "E191", {"start": v(-57.92, 33.94) * mm, "end": v(-57.61, 33.94) * mm});
            skFitSpline(sketch, "E192", {"points": [v(-49.47, 21.3) * mm, v(-47.54, 23.85) * mm, v(-45.96, 23.95) * mm, v(-44.18, 25.01) * mm, v(-42.6, 24.76) * mm, v(-42.46, 26.23) * mm, v(-41.49, 27.6) * mm, v(-40.27, 27.5) * mm, v(-39.46, 28.37) * mm, v(-38.24, 28.62) * mm, v(-37.37, 27.81) * mm, v(-36.2, 27.86) * mm, v(-35.08, 27.2) * mm, v(-34.17, 26.23) * mm, v(-33.3, 25.93) * mm, v(-32.85, 23.74) * mm, v(-32.34, 23.64) * mm, v(-31.42, 21.56) * mm, v(-31.68, 20.75) * mm, v(-31.07, 19.68) * mm], "startDerivative": vector(23.16, 43.64) * mm, "endDerivative": vector(19.02, -23.88) * mm});
            skFitSpline(sketch, "E193", {"points": [v(-31.07, 19.68) * mm, v(-30.84, 18.57) * mm, v(-31.63, 17.95) * mm, v(-32.14, 16.58) * mm, v(-32.02, 15.22) * mm, v(-33.08, 14.55) * mm, v(-33.26, 13.16) * mm], "startDerivative": vector(3.34, -8.02) * mm, "endDerivative": vector(1, -9.25) * mm});
            skFitSpline(sketch, "E194", {"points": [v(-33.26, 12.92) * mm, v(-33.77, 12.74) * mm, v(-34.02, 11.68) * mm, v(-34.2, 10.86) * mm, v(-34.44, 9.99) * mm, v(-35.22, 8.8) * mm, v(-35.13, 8.11) * mm, v(-34.98, 4.4) * mm], "startDerivative": vector(-6.09, -0.49) * mm, "endDerivative": vector(-0.04, -17.77) * mm});
            skFitSpline(sketch, "E195", {"points": [v(-34.98, 4.4) * mm, v(-34.23, 3.67) * mm, v(-34.26, 1.74) * mm, v(-34.4, 0.53) * mm, v(-34.98, -0.44) * mm, v(-34.98, -2.56) * mm, v(-33.32, -4.88) * mm], "startDerivative": vector(7.07, -4.14) * mm, "endDerivative": vector(9.35, -10.07) * mm});
            skFitSpline(sketch, "E196", {"points": [v(-33.32, -4.88) * mm, v(-32.53, -6.49) * mm, v(-32.75, -9.69) * mm, v(-34.38, -13.29) * mm], "startDerivative": vector(3.63, -5.45) * mm, "endDerivative": vector(-4.92, -9.04) * mm});
            skFitSpline(sketch, "E197", {"points": [v(-34.38, -13.29) * mm, v(-34.05, -15.07) * mm, v(-33.32, -16.43) * mm, v(-33.32, -18.88) * mm], "startDerivative": vector(0.5, -5.88) * mm, "endDerivative": vector(-0.82, -7.14) * mm});
            skFitSpline(sketch, "E198", {"points": [v(-33.32, -18.88) * mm, v(-34.38, -20.33) * mm, v(-33.92, -21.63) * mm, v(-34.08, -25.74) * mm], "startDerivative": vector(-5.19, -5.1) * mm, "endDerivative": vector(-1.44, -10.58) * mm});
            skFitSpline(sketch, "E199", {"points": [v(-34.08, -25.74) * mm, v(-34.08, -28.94) * mm], "startDerivative": vector(0, -3.2) * mm, "endDerivative": vector(0, -3.2) * mm});
            skFitSpline(sketch, "E200", {"points": [v(-34.08, -28.94) * mm, v(-33.86, -30.54) * mm, v(-34.95, -32.24) * mm], "startDerivative": vector(1.04, -3.43) * mm, "endDerivative": vector(-2.73, -3.16) * mm});
            skFitSpline(sketch, "E201", {"points": [v(-34.95, -32.24) * mm, v(-35.32, -34.14) * mm, v(-36.28, -35.92) * mm, v(-35.98, -37.77) * mm], "startDerivative": vector(-0.37, -5.88) * mm, "endDerivative": vector(2.03, -5.78) * mm});
            skFitSpline(sketch, "E202", {"points": [v(-35.98, -37.77) * mm, v(-36.86, -39.1) * mm, v(-38.1, -39) * mm, v(-38.22, -36.47) * mm, v(-38.88, -35.74) * mm, v(-39.06, -33.72) * mm], "startDerivative": vector(-3.18, -8.02) * mm, "endDerivative": vector(0.65, 10.95) * mm});
            skFitSpline(sketch, "E203", {"points": [v(-39.06, -33.72) * mm, v(-38.82, -30.4) * mm, v(-39.76, -29.27) * mm, v(-39.73, -26.46) * mm, v(-39.06, -26.1) * mm, v(-38.73, -24.14) * mm], "startDerivative": vector(3.19, 15.34) * mm, "endDerivative": vector(0.27, 12.58) * mm});
            skFitSpline(sketch, "E204", {"points": [v(-38.73, -24.14) * mm, v(-38.73, -23.18) * mm, v(-39.26, -22.45) * mm, v(-38.92, -20.8) * mm], "startDerivative": vector(0.63, 3.44) * mm, "endDerivative": vector(1.8, 4.66) * mm});
            skFitSpline(sketch, "E205", {"points": [v(-38.92, -20.8) * mm, v(-38.33, -17.07) * mm, v(-38.43, -15.64) * mm, v(-38.38, -13) * mm, v(-38.12, -11.53) * mm, v(-38.22, -10) * mm, v(-38.92, -8.48) * mm, v(-39.7, -6.44) * mm], "startDerivative": vector(4.35, 21.95) * mm, "endDerivative": vector(-4.97, 14.41) * mm});
            skFitSpline(sketch, "E206", {"points": [v(-39.7, -6.44) * mm, v(-39.7, -4.41) * mm, v(-39.09, -2.78) * mm, v(-39.7, -1.06) * mm, v(-40.51, 0.72) * mm, v(-40.87, 2.05) * mm, v(-40.71, 4.08) * mm], "startDerivative": vector(-1.55, 11.99) * mm, "endDerivative": vector(1.7, 12.3) * mm});
            skFitSpline(sketch, "E207", {"points": [v(-40.71, 4.08) * mm, v(-40.71, 5.8) * mm, v(-41.38, 6.98) * mm, v(-41.99, 7.53) * mm, v(-39.7, 10.13) * mm, v(-40.36, 11.04) * mm, v(-40.2, 12.47) * mm], "startDerivative": vector(0.86, 10.16) * mm, "endDerivative": vector(3.6, 9.96) * mm});
            skFitSpline(sketch, "E208", {"points": [v(-40.2, 12.47) * mm, v(-40.2, 17.45) * mm, v(-40.4, 18.7) * mm, v(-41.37, 19.08) * mm, v(-42.1, 19.13) * mm, v(-43.63, 19.17) * mm, v(-45.5, 19.41) * mm, v(-46.56, 20.42) * mm], "startDerivative": vector(-0.2, 23.17) * mm, "endDerivative": vector(-6.8, 8.98) * mm});
            skFitSpline(sketch, "E209", {"points": [v(-46.56, 20.42) * mm, v(-48.24, 20.42) * mm, v(-49.24, 20.42) * mm, v(-49.47, 21.3) * mm], "startDerivative": vector(-4.31, 0.23) * mm, "endDerivative": vector(-0.18, 3.79) * mm});
            skFitSpline(sketch, "E210", {"points": [v(-82.85, 22.32) * mm, v(-85.57, 22.38) * mm, v(-86.78, 22.14) * mm, v(-87.33, 22.87) * mm, v(-86.48, 24.02) * mm, v(-84.37, 24.86) * mm, v(-82.07, 26.07) * mm, v(-77.84, 26.25) * mm, v(-76.5, 27.34) * mm, v(-74.15, 28.67) * mm, v(-73.25, 28.63) * mm, v(-72.83, 27.63) * mm, v(-71.46, 27.19) * mm, v(-68.86, 26.96) * mm, v(-68.2, 26.48) * mm, v(-67.65, 26.96) * mm, v(-66.88, 26.96) * mm, v(-65.66, 28.05) * mm, v(-64.67, 28.5) * mm, v(-62.27, 28.34) * mm, v(-61.56, 29.46) * mm, v(-58.78, 29.68) * mm, v(-56.02, 31.35) * mm], "startDerivative": vector(-52.25, 5.76) * mm, "endDerivative": vector(40.09, 36.15) * mm});
            skFitSpline(sketch, "E211", {"points": [v(-56.02, 31.35) * mm, v(-55.54, 31.73) * mm, v(-55, 31.9) * mm, v(-54.33, 31.35) * mm, v(-53.1, 30.07) * mm, v(-52.72, 29.97) * mm, v(-51.67, 29.4) * mm, v(-51.22, 28.85) * mm, v(-50.42, 28.53) * mm, v(-49.2, 28.72) * mm, v(-49.07, 27.12) * mm, v(-47.31, 26.38) * mm, v(-46.96, 24.88) * mm, v(-48.24, 24.34) * mm, v(-49.14, 24.02) * mm, v(-49.78, 23.09) * mm, v(-49.94, 21.55) * mm, v(-50.2, 20.72) * mm, v(-51.19, 20.3) * mm], "startDerivative": vector(10.82, 9.8) * mm, "endDerivative": vector(-21.15, -5.45) * mm});
            skFitSpline(sketch, "E212", {"points": [v(-51.19, 20.3) * mm, v(-51.19, 18.93) * mm, v(-51.73, 18.72) * mm, v(-51.46, 17.9) * mm, v(-51.4, 16.13) * mm, v(-51.76, 15.51) * mm, v(-50.81, 14.25) * mm, v(-50.5, 12.8) * mm, v(-51.13, 12.07) * mm], "startDerivative": vector(2.55, -12.5) * mm, "endDerivative": vector(-4.38, -5.98) * mm});
            skFitSpline(sketch, "E213", {"points": [v(-51.13, 12.07) * mm, v(-51.13, 10.7) * mm, v(-50.17, 9.16) * mm, v(-50.29, 6.1) * mm], "startDerivative": vector(-0.66, -4.72) * mm, "endDerivative": vector(-0.68, -6.44) * mm});
            skFitSpline(sketch, "E214", {"points": [v(-50.29, 6.1) * mm, v(-51.13, 4.62) * mm, v(-51.13, 3.02) * mm, v(-51.19, 1.36) * mm, v(-51.13, -0.5) * mm, v(-50.5, -2.2) * mm], "startDerivative": vector(-4.5, -9.3) * mm, "endDerivative": vector(1.76, -8.58) * mm});
            skFitSpline(sketch, "E215", {"points": [v(-50.5, -2.2) * mm, v(-49.71, -4.03) * mm, v(-49.98, -7.8) * mm, v(-50.76, -8.55) * mm, v(-51.2, -9.02) * mm, v(-51.61, -9.73) * mm, v(-51.51, -11.43) * mm], "startDerivative": vector(4.76, -9.72) * mm, "endDerivative": vector(1.8, -10.73) * mm});
            skFitSpline(sketch, "E216", {"points": [v(-51.51, -11.43) * mm, v(-51.92, -12.14) * mm, v(-51.92, -13.23) * mm, v(-52.4, -13.63) * mm, v(-53, -15.77) * mm, v(-52.26, -16.32) * mm], "startDerivative": vector(-3.14, -3.45) * mm, "endDerivative": vector(5.24, -1.54) * mm});
            skFitSpline(sketch, "E217", {"points": [v(-52.26, -16.32) * mm, v(-52.26, -17.47) * mm, v(-52.26, -18.08) * mm, v(-52.7, -19) * mm, v(-52.26, -19.23) * mm, v(-51.99, -20.32) * mm, v(-52.66, -21.13) * mm, v(-52.26, -22.05) * mm, v(-51.95, -23.58) * mm, v(-51.95, -24.66) * mm, v(-52.77, -25.3) * mm], "startDerivative": vector(-0.56, -11.85) * mm, "endDerivative": vector(-10, -5.4) * mm});
            skFitSpline(sketch, "E218", {"points": [v(-52.77, -25.3) * mm, v(-52.77, -29.1) * mm, v(-52.77, -30.2) * mm, v(-51.07, -33.48) * mm, v(-51.51, -35.31) * mm], "startDerivative": vector(0.5, -14.5) * mm, "endDerivative": vector(-4.2, -7.45) * mm});
            skFitSpline(sketch, "E219", {"points": [v(-51.51, -35.31) * mm, v(-51.51, -37.32) * mm, v(-51.95, -37.76) * mm, v(-52.09, -43.9) * mm, v(-52.3, -44.6) * mm, v(-53.65, -46.5) * mm, v(-54.6, -46.95) * mm, v(-55.55, -47.02) * mm, v(-55.55, -44.98) * mm, v(-55, -42.6) * mm, v(-54.56, -41.15) * mm, v(-55.48, -39.8) * mm, v(-55.79, -38.16) * mm, v(-56.9, -37.08) * mm, v(-56.84, -35) * mm, v(-56.36, -34.26) * mm, v(-56.43, -33.21) * mm, v(-56.77, -32.12) * mm], "startDerivative": vector(4.5, -39.22) * mm, "endDerivative": vector(-7.38, 21.26) * mm});
            skFitSpline(sketch, "E220", {"points": [v(-56.77, -32.12) * mm, v(-56.84, -26.66) * mm, v(-57.45, -25.88) * mm, v(-58.06, -24.08) * mm, v(-57.82, -21.4) * mm], "startDerivative": vector(1.18, 18.65) * mm, "endDerivative": vector(1.87, 10.57) * mm});
            skFitSpline(sketch, "E221", {"points": [v(-57.82, -21.4) * mm, v(-57.82, -20.42) * mm, v(-58.87, -19.33) * mm, v(-59.38, -17.4) * mm, v(-58.67, -15.98) * mm, v(-58.47, -14.21) * mm, v(-57.82, -13.57) * mm, v(-57.48, -10.31) * mm], "startDerivative": vector(1.95, 9.47) * mm, "endDerivative": vector(-0.28, 20.14) * mm});
            skFitSpline(sketch, "E222", {"points": [v(-57.48, -10.31) * mm, v(-56.77, -8.55) * mm, v(-56.65, -7.6) * mm, v(-57.46, -5.02) * mm, v(-57.82, -3.2) * mm, v(-57.82, 0) * mm, v(-57.82, 2.74) * mm, v(-58.2, 3.91) * mm, v(-58.58, 4.94) * mm, v(-58.49, 6.64) * mm, v(-58.4, 7.79) * mm, v(-58.68, 9.1) * mm, v(-59.13, 9.97) * mm, v(-59.15, 13.18) * mm, v(-58.8, 14.43) * mm, v(-59.6, 15) * mm, v(-60.8, 16.54) * mm, v(-60.4, 18.31) * mm, v(-60.29, 20.14) * mm, v(-60.63, 20.94) * mm, v(-60.8, 22.08) * mm, v(-60.97, 22.36) * mm, v(-61.37, 22.7) * mm, v(-61.94, 23.8) * mm, v(-62.68, 23.33) * mm, v(-65.25, 23.8) * mm, v(-66.1, 23.56) * mm, v(-66.28, 21.62) * mm, v(-66.73, 20.94) * mm, v(-66.33, 19.34) * mm, v(-66.9, 18.6) * mm, v(-68.33, 17.69) * mm, v(-68.62, 14.83) * mm, v(-67.82, 13.35) * mm, v(-68.62, 10.5) * mm, v(-68.96, 7.93) * mm, v(-68.5, 6.37) * mm, v(-68.8, 4.06) * mm, v(-67.9, 2.7) * mm, v(-67.81, 1.5) * mm, v(-65.63, -2.05) * mm, v(-66.54, -4.77) * mm, v(-66.92, -6.7) * mm, v(-66.86, -9.48) * mm, v(-65.58, -11.66) * mm, v(-65.96, -14.3) * mm, v(-67.01, -17.27) * mm, v(-67.5, -21.4) * mm, v(-66.44, -25.04) * mm, v(-67.11, -26.48) * mm, v(-66.73, -28.11) * mm, v(-67.11, -29.36) * mm, v(-66.63, -30.32) * mm, v(-66.82, -33.87) * mm, v(-66.15, -37.7) * mm, v(-65.38, -39.24) * mm, v(-65.67, -42.02) * mm], "startDerivative": vector(45.23, 107.74) * mm, "endDerivative": vector(-30.31, -141.1) * mm});
            skFitSpline(sketch, "E223", {"points": [v(-65.67, -42.02) * mm, v(-66.92, -42.02) * mm, v(-67.55, -40.24) * mm, v(-67.55, -39.15) * mm, v(-68.74, -37.84) * mm, v(-68.92, -34.87) * mm, v(-69.2, -32.42) * mm, v(-70.34, -28.48) * mm, v(-71.94, -26.2) * mm, v(-71.03, -24.77) * mm, v(-72.34, -23.23) * mm, v(-72, -21.47) * mm, v(-73.42, -20.04) * mm, v(-72.97, -17.81) * mm, v(-72.9, -16.39) * mm, v(-72, -15.36) * mm, v(-72.28, -10.62) * mm, v(-73.25, -9.31) * mm, v(-72.85, -7.83) * mm, v(-73.02, -4.7) * mm, v(-74.4, 0) * mm, v(-76.85, 4.67) * mm, v(-75.88, 10.77) * mm, v(-75.48, 12.08) * mm, v(-76.1, 13.22) * mm, v(-75.48, 14.25) * mm, v(-75.76, 15.4) * mm, v(-76, 16.53) * mm, v(-77.99, 18.47) * mm, v(-77.47, 19.56) * mm, v(-79.13, 21.55) * mm, v(-81.58, 21.95) * mm, v(-82.85, 22.32) * mm], "startDerivative": vector(-58.06, -15.7) * mm, "endDerivative": vector(-47.66, 19.1) * mm});
            skLineSegment(sketch, "E224", {"start": v(-33.26, 13.16) * mm, "end": v(-33.26, 12.92) * mm});
            skSolve(sketch);
        }
        {
            var Q0;
            Q0 = qSketchRegion(id + "F2", true);
            var Q1;
            Q1 = qConstructionFilter(qBodyType(qCreatedBy(id + "F2" ,EDGE), BodyType.WIRE), ConstructionObject.NO);
            extrude(context, id + "F3", {"entities" : qUnion([Q0]), "surfaceEntities" : qUnion([Q1]), "depth" : 25 * mm});
        }
    });
